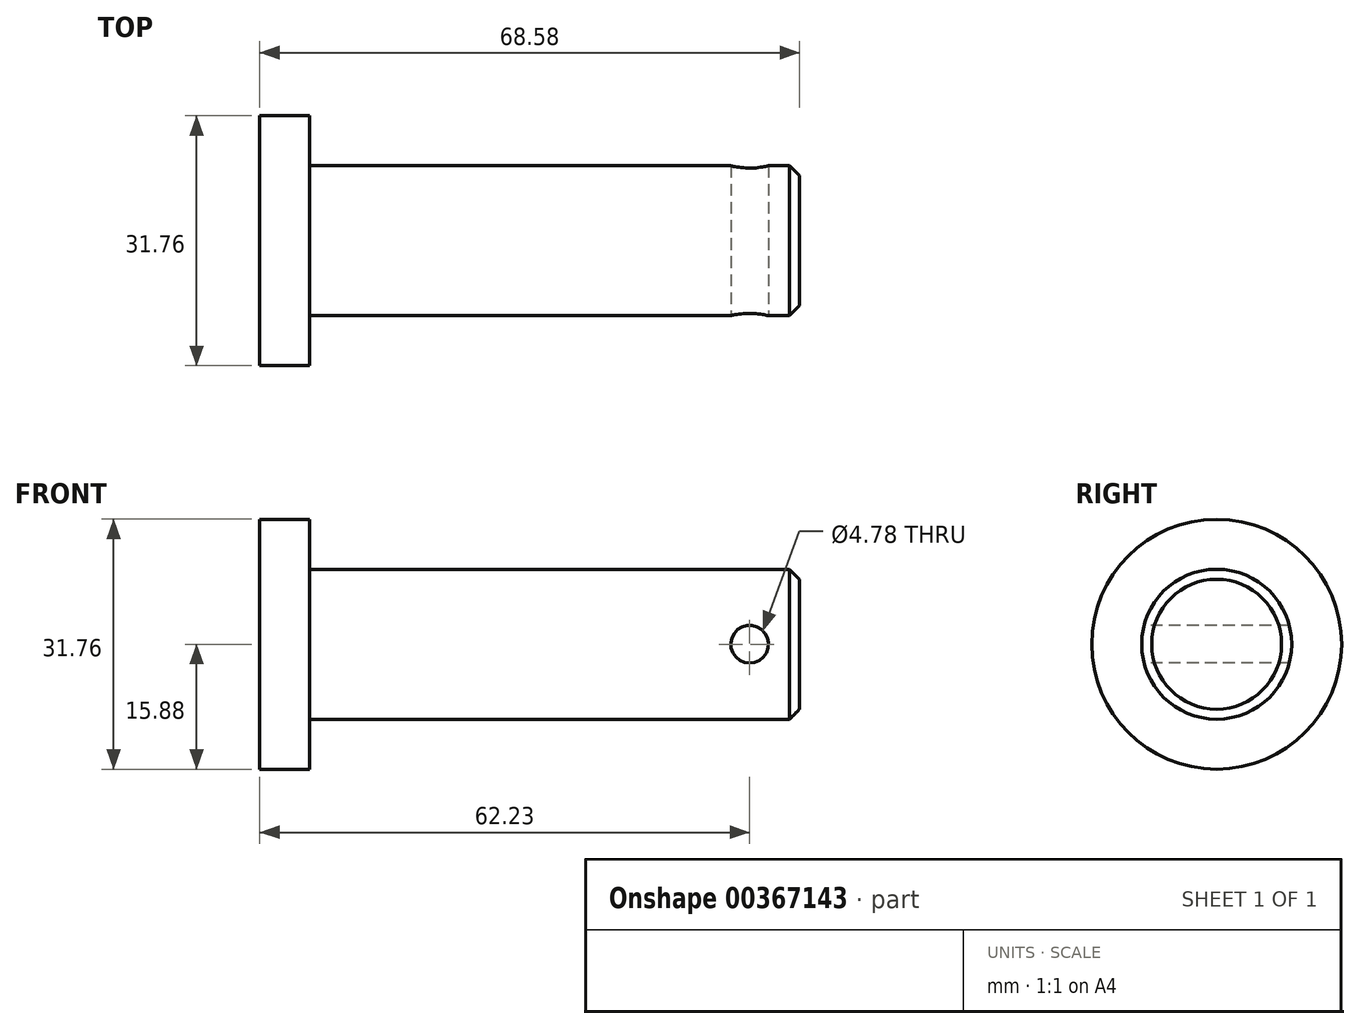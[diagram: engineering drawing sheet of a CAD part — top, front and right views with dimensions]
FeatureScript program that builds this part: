
annotation { "Feature Type Name" : "Feature", "Feature Type Description" : "" }
export const myFeature = defineFeature(function(context is Context, id is Id, definition is map)
    precondition{}
    {
        {
            var Q0;
            Q0=qCreatedBy(makeId("Right.planeOp"),FACE);
            var sketch = newSketch(context, id + "F0", { "sketchPlane" : qUnion([Q0])});
            skCircle(sketch, "E0", {"center": v(0, 0) * mm, "radius": 15.88 * mm});
            skSolve(sketch);
        }
        {
            var Q0;
            Q0 = qSketchRegion(id + "F0", true);
            extrude(context, id + "F1", {"entities" : qUnion([Q0]), "depth" : 6.35 * mm});
        }
        {
            var Q0;
            Q0=makeQuery(id+"F1.opExtrude","CAP_FACE",FACE,{"disambiguationData":[OSD([sQuery(id+"F0.wireOp",EDGE,"E0")])],"isStart":false});
            var sketch = newSketch(context, id + "F2", { "sketchPlane" : qUnion([Q0])});
            skCircle(sketch, "E1", {"center": v(0, 0) * mm, "radius": 9.53 * mm});
            skSolve(sketch);
        }
        {
            var Q0;
            Q0 = qSketchRegion(id + "F2", true);
            extrude(context, id + "F3", {"entities" : qUnion([Q0]), "operationType" : NewBodyOperationType.ADD, "depth" : 62.23 * mm});
        }
        {
            var Q0;
            Q0=qCreatedBy(makeId("Front.planeOp"),FACE);
            var sketch = newSketch(context, id + "F4", { "sketchPlane" : qUnion([Q0])});
            skCircle(sketch, "E2", {"center": v(62.23, 0) * mm, "radius": 2.39 * mm});
            skSolve(sketch);
        }
        {
            var Q0;
            Q0 = qSketchRegion(id + "F4", true);
            extrude(context, id + "F5", {"entities" : qUnion([Q0]), "operationType" : NewBodyOperationType.REMOVE, "endBound" : BoundingType.THROUGH_ALL, "oppositeDirection" : true, "depth" : 25.4 * mm, "hasSecondDirection" : true, "secondDirectionOppositeDirection" : false, "secondDirectionDepth" : 25.4 * mm});
        }
        {
            var Q0;
            Q0=makeQuery(id+"F3.opExtrude","CAP_EDGE",EDGE,{"disambiguationData":[OSD([sQuery(id+"F2.wireOp",EDGE,"E1")])],"isStart":false});
            chamfer(context, id + "F6", {"entities" : qUnion([Q0]), "width" : 1.27 * mm, "tangentPropagation" : true});
        }
    });
